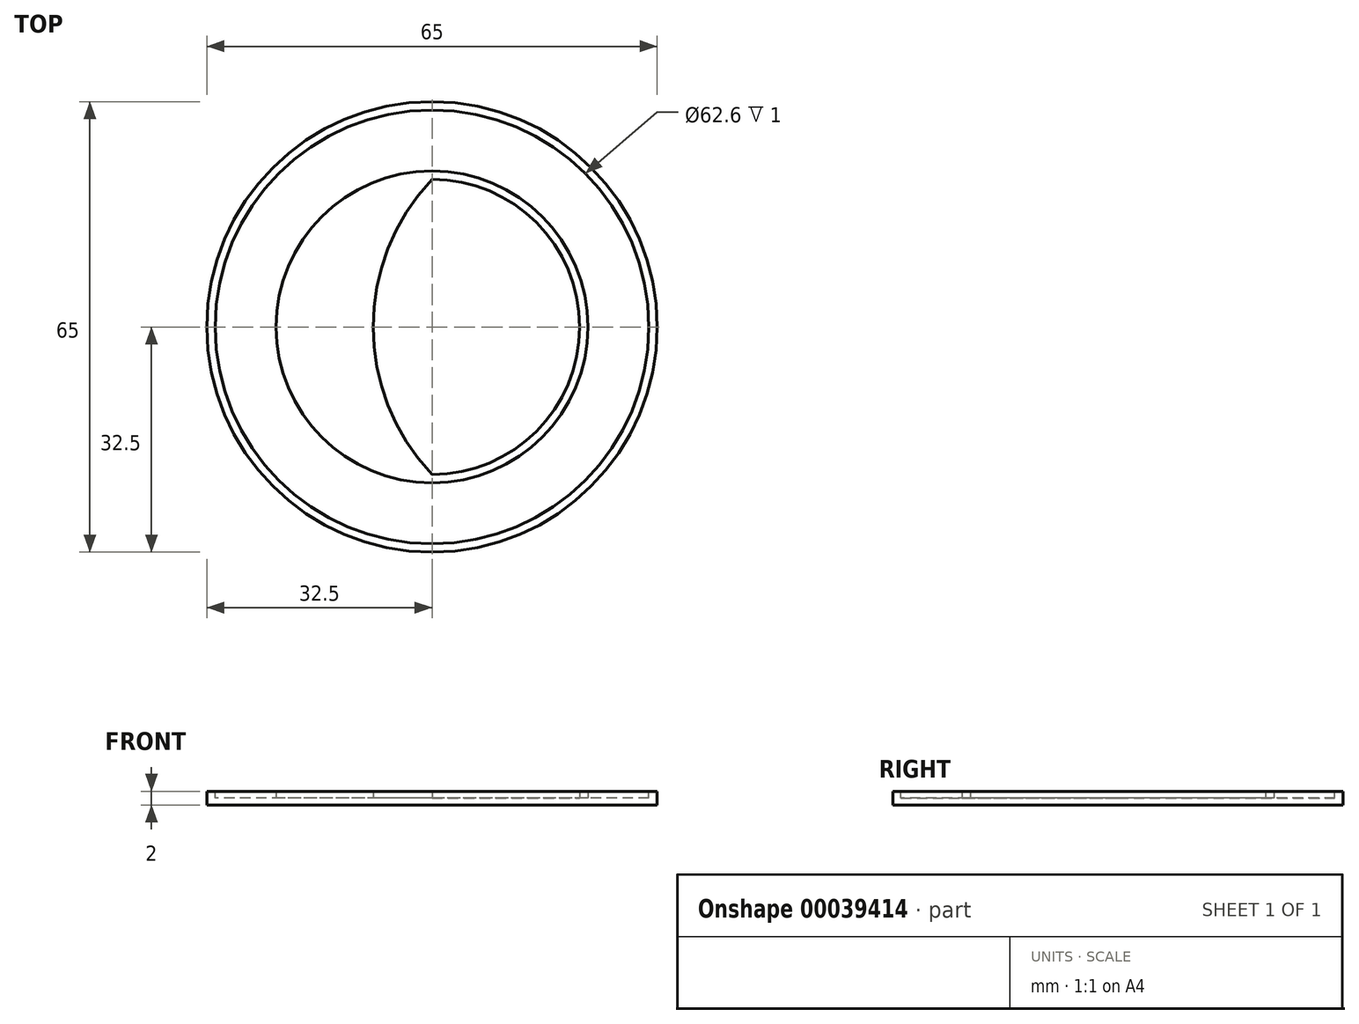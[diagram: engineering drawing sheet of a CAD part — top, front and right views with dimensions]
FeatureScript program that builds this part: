
annotation { "Feature Type Name" : "Feature", "Feature Type Description" : "" }
export const myFeature = defineFeature(function(context is Context, id is Id, definition is map)
    precondition{}
    {
        {
            var Q0;
            Q0=qCreatedBy(makeId("Top.planeOp"),FACE);
            var sketch = newSketch(context, id + "F0", { "sketchPlane" : qUnion([Q0])});
            skCircle(sketch, "E0", {"center": v(0, 0) * mm, "radius": 32.5 * mm});
            skSolve(sketch);
        }
        {
            var Q0;
            Q0=qSketchRegion(id+"F0",true);
            extrude(context, id + "F1", {"entities" : qUnion([Q0]), "depth" : 2 * mm});
        }
        {
            var Q0;
            Q0=makeQuery(id+"F1.opExtrude","CAP_FACE",FACE,{"disambiguationData":[OSD([sQuery(id+"F0.wireOp",EDGE,"E0")])],"isStart":false});
            var sketch = newSketch(context, id + "F2", { "sketchPlane" : qUnion([Q0])});
            skCircle(sketch, "E1", {"center": v(0, 0) * mm, "radius": 31.3 * mm});
            skSolve(sketch);
        }
        {
            var Q0;
            Q0=qSketchRegion(id+"F2",true);
            extrude(context, id + "F3", {"entities" : qUnion([Q0]), "operationType" : NewBodyOperationType.REMOVE, "oppositeDirection" : true, "depth" : 1 * mm});
        }
        {
            var Q0;
            Q0=makeQuery(id+"F3.boolean.opBoolean","COPY",FACE,{"derivedFrom":makeQuery(id+"F3.opExtrude","CAP_FACE",FACE,{"disambiguationData":[OSD([sQuery(id+"F2.wireOp",EDGE,"E1")])],"isStart":false})});
            var sketch = newSketch(context, id + "F4", { "sketchPlane" : qUnion([Q0])});
            skCircle(sketch, "E2", {"center": v(0, 0) * mm, "radius": 22.5 * mm});
            skArc(sketch, "E3", {"start": v(0, 21.3) * mm, "mid": v(-8.48, 0) * mm, "end": v(0, -21.3) * mm});
            skArc(sketch, "E4", {"start": v(0, -21.3) * mm, "mid": v(21.3, 0) * mm, "end": v(0, 21.3) * mm});
            skSolve(sketch);
        }
        {
            var Q0;
            Q0=qSketchRegion(id+"F4",true);
            extrude(context, id + "F5", {"entities" : qUnion([Q0]), "operationType" : NewBodyOperationType.ADD, "depth" : 1 * mm});
        }
    });
